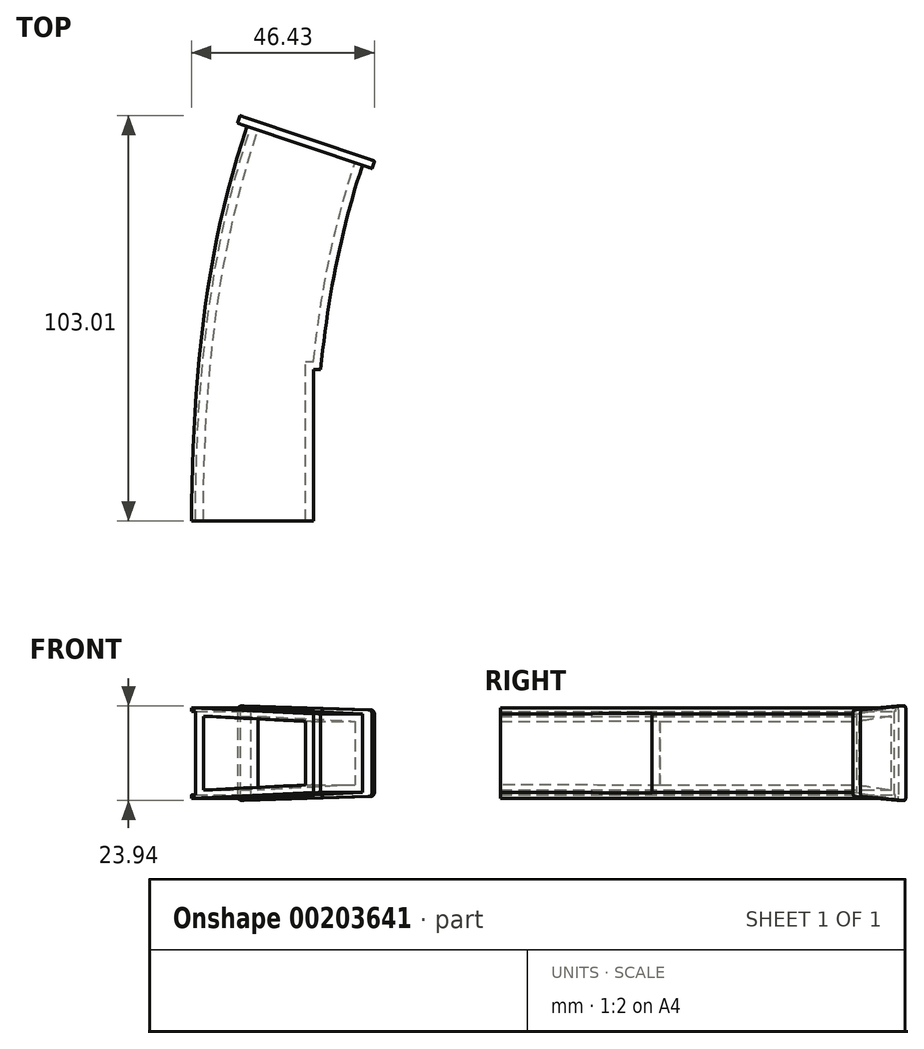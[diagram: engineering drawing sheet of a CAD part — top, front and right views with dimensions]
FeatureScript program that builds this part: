
annotation { "Feature Type Name" : "Feature", "Feature Type Description" : "" }
export const myFeature = defineFeature(function(context is Context, id is Id, definition is map)
    precondition{}
    {
        {
            var Q0;
            Q0=qCreatedBy(makeId("Front.planeOp"),FACE);
            var sketch = newSketch(context, id + "F0", { "sketchPlane" : qUnion([Q0])});
            skLineSegment(sketch, "E0.bottom", {"start": v(0, 10) * mm, "end": v(30, 10) * mm});
            skLineSegment(sketch, "E0.top", {"start": v(0, -10) * mm, "end": v(30, -10) * mm});
            skLineSegment(sketch, "E0.left", {"start": v(0, 10) * mm, "end": v(0, -10) * mm});
            skLineSegment(sketch, "E0.right", {"start": v(30, 10) * mm, "end": v(30, -10) * mm});
            skLineSegment(sketch, "E1", {"start": v(30, 10) * mm, "end": v(0, 11.5) * mm});
            skLineSegment(sketch, "E2", {"start": v(0, 11.5) * mm, "end": v(0, 10) * mm});
            skLineSegment(sketch, "E3", {"start": v(0, -10) * mm, "end": v(0, -11.5) * mm});
            skLineSegment(sketch, "E4", {"start": v(0, -11.5) * mm, "end": v(30, -10) * mm});
            skLineSegment(sketch, "E5", {"start": v(0, 11.5) * mm, "end": v(-1, 11.55) * mm});
            skLineSegment(sketch, "E6", {"start": v(-1, 11.55) * mm, "end": v(-1, 10.55) * mm});
            skLineSegment(sketch, "E7", {"start": v(-1, 10.55) * mm, "end": v(0, 10.55) * mm});
            skLineSegment(sketch, "E8", {"start": v(0, -11.5) * mm, "end": v(-1, -11.55) * mm});
            skLineSegment(sketch, "E9", {"start": v(-1, -11.55) * mm, "end": v(-1, -10.55) * mm});
            skLineSegment(sketch, "E10", {"start": v(-1, -10.55) * mm, "end": v(0, -10.55) * mm});
            skSolve(sketch);
        }
        {
            var Q0;
            Q0=qCreatedBy(makeId("Top.planeOp"),FACE);
            var sketch = newSketch(context, id + "F1", { "sketchPlane" : qUnion([Q0])});
            skFitSpline(sketch, "E11", {"points": [v(0, 0) * mm, v(14, 100) * mm], "startDerivative": vector(0, 107.41) * mm, "endDerivative": vector(30.73, 90.98) * mm});
            skSolve(sketch);
        }
        {
            var Q0;
            Q0=makeQuery(id+"F0.imprint","IMPRINT",FACE,{"disambiguationData":[TD([[makeQuery(id+"F0.imprint","IMPRINT",EDGE,{"derivedFrom":sQuery(id+"F0.wireOp",EDGE,"E0.bottom")}),-1.0]])]});
            var Q1;
            {var subQ0=sQuery(id+"F0.wireOp",EDGE,"E0.bottom");Q1=makeQuery(id+"F0.imprint","IMPRINT",FACE,{"disambiguationData":[TD([[makeQuery(id+"F0.imprint","IMPRINT",EDGE,{"derivedFrom":subQ0}),1.0]])]});}
            var Q2;
            {var subQ0=sQuery(id+"F0.wireOp",EDGE,"E5");Q2=makeQuery(id+"F0.imprint","IMPRINT",FACE,{"disambiguationData":[TD([[makeQuery(id+"F0.imprint","IMPRINT",EDGE,{"derivedFrom":subQ0}),1.0]])]});}
            var Q3;
            {var subQ0=sQuery(id+"F0.wireOp",EDGE,"E8");Q3=makeQuery(id+"F0.imprint","IMPRINT",FACE,{"disambiguationData":[TD([[makeQuery(id+"F0.imprint","IMPRINT",EDGE,{"derivedFrom":subQ0}),-1.0]])]});}
            var Q4;
            {var subQ0=sQuery(id+"F0.wireOp",EDGE,"E0.top");Q4=makeQuery(id+"F0.imprint","IMPRINT",FACE,{"disambiguationData":[TD([[makeQuery(id+"F0.imprint","IMPRINT",EDGE,{"derivedFrom":subQ0}),-1.0]])]});}
            var Q5;
            Q5 = qConstructionFilter(qBodyType(qCreatedBy(id + "F0" ,EDGE), BodyType.WIRE), ConstructionObject.NO);
            var Q6;
            Q6 = qConstructionFilter(qBodyType(qCreatedBy(id + "F1" ,EDGE), BodyType.WIRE), ConstructionObject.NO);
            sweep(context, id + "F2", {"profiles" : qUnion([Q0, Q1, Q2, Q3, Q4]), "surfaceProfiles" : qUnion([Q5]), "path" : qUnion([Q6])});
        }
        {
            var Q0;
            Q0=makeQuery(id+"F2.opSweep","CAP_FACE",FACE,{"disambiguationData":[OSD([sQuery(id+"F0.wireOp",EDGE,"E0.left"),sQuery(id+"F0.wireOp",EDGE,"E0.right"),sQuery(id+"F0.wireOp",EDGE,"E1"),sQuery(id+"F0.wireOp",EDGE,"E2"),sQuery(id+"F0.wireOp",EDGE,"E3"),sQuery(id+"F0.wireOp",EDGE,"E4"),sQuery(id+"F0.wireOp",EDGE,"E5"),sQuery(id+"F0.wireOp",EDGE,"E6"),sQuery(id+"F0.wireOp",EDGE,"E7"),sQuery(id+"F0.wireOp",EDGE,"E8"),sQuery(id+"F0.wireOp",EDGE,"E9"),sQuery(id+"F0.wireOp",EDGE,"E10"),sQuery(id+"F1.wireOp",VERTEX,"E11.end")])],"isStart":false});
            var sketch = newSketch(context, id + "F3", { "sketchPlane" : qUnion([Q0])});
            skLineSegment(sketch, "E12.left", {"start": v(-13.76, 10.03) * mm, "end": v(-13.76, -10.03) * mm});
            skLineSegment(sketch, "E13", {"start": v(-12.8, 11.03) * mm, "end": v(21.2, 11.97) * mm});
            skLineSegment(sketch, "E14", {"start": v(-12.8, -11.03) * mm, "end": v(21.2, -11.97) * mm});
            skLineSegment(sketch, "E15", {"start": v(22.24, 10.97) * mm, "end": v(22.24, -10.97) * mm});
            skPoint(sketch, "E16.visualSharp", {"position": v(22.24, 12) * mm});
            skArc(sketch, "E16.filletArc", {"start": v(22.24, 10.97) * mm, "mid": v(21.93, 11.69) * mm, "end": v(21.2, 11.97) * mm});
            skPoint(sketch, "E17.visualSharp", {"position": v(22.24, -12) * mm});
            skArc(sketch, "E17.filletArc", {"start": v(21.2, -11.97) * mm, "mid": v(21.93, -11.69) * mm, "end": v(22.24, -10.97) * mm});
            skPoint(sketch, "E18.visualSharp", {"position": v(-13.76, -11) * mm});
            skArc(sketch, "E18.filletArc", {"start": v(-13.76, -10.03) * mm, "mid": v(-13.48, -10.72) * mm, "end": v(-12.8, -11.03) * mm});
            skPoint(sketch, "E19.visualSharp", {"position": v(-13.76, 11) * mm});
            skArc(sketch, "E19.filletArc", {"start": v(-12.8, 11.03) * mm, "mid": v(-13.48, 10.72) * mm, "end": v(-13.76, 10.03) * mm});
            skSolve(sketch);
        }
        {
            var Q0;
            Q0 = qSketchRegion(id + "F3", true);
            extrude(context, id + "F4", {"entities" : qUnion([Q0]), "operationType" : NewBodyOperationType.ADD, "depth" : 2 * mm});
        }
        {
            var Q0;
            Q0=qCreatedBy(makeId("Top.planeOp"),FACE);
            var sketch = newSketch(context, id + "F5", { "sketchPlane" : qUnion([Q0])});
            skLineSegment(sketch, "E20.bottom", {"start": v(30, 0) * mm, "end": v(33, 0) * mm});
            skLineSegment(sketch, "E20.top", {"start": v(30, 38.5) * mm, "end": v(33, 38.5) * mm});
            skLineSegment(sketch, "E20.left", {"start": v(30, 0) * mm, "end": v(30, 38.5) * mm});
            skLineSegment(sketch, "E20.right", {"start": v(33, 0) * mm, "end": v(33, 38.5) * mm});
            skSolve(sketch);
        }
        {
            var Q0;
            Q0 = qSketchRegion(id + "F5", true);
            extrude(context, id + "F6", {"entities" : qUnion([Q0]), "operationType" : NewBodyOperationType.REMOVE, "oppositeDirection" : true, "depth" : 25 * mm, "hasSecondDirection" : true, "secondDirectionOppositeDirection" : false, "secondDirectionDepth" : 25 * mm});
        }
        {
            var Q0;
            Q0=makeQuery(id+"F2.opSweep","CAP_FACE",FACE,{"disambiguationData":[OSD([sQuery(id+"F0.wireOp",EDGE,"E0.left"),sQuery(id+"F0.wireOp",EDGE,"E0.right"),sQuery(id+"F0.wireOp",EDGE,"E1"),sQuery(id+"F0.wireOp",EDGE,"E2"),sQuery(id+"F0.wireOp",EDGE,"E3"),sQuery(id+"F0.wireOp",EDGE,"E4"),sQuery(id+"F0.wireOp",EDGE,"E5"),sQuery(id+"F0.wireOp",EDGE,"E6"),sQuery(id+"F0.wireOp",EDGE,"E7"),sQuery(id+"F0.wireOp",EDGE,"E8"),sQuery(id+"F0.wireOp",EDGE,"E9"),sQuery(id+"F0.wireOp",EDGE,"E10"),sQuery(id+"F1.wireOp",VERTEX,"E11.start")])],"isStart":true});
            shell(context, id + "F7", {"entities" : qUnion([Q0]), "thickness" : 2 * mm});
        }
    });
